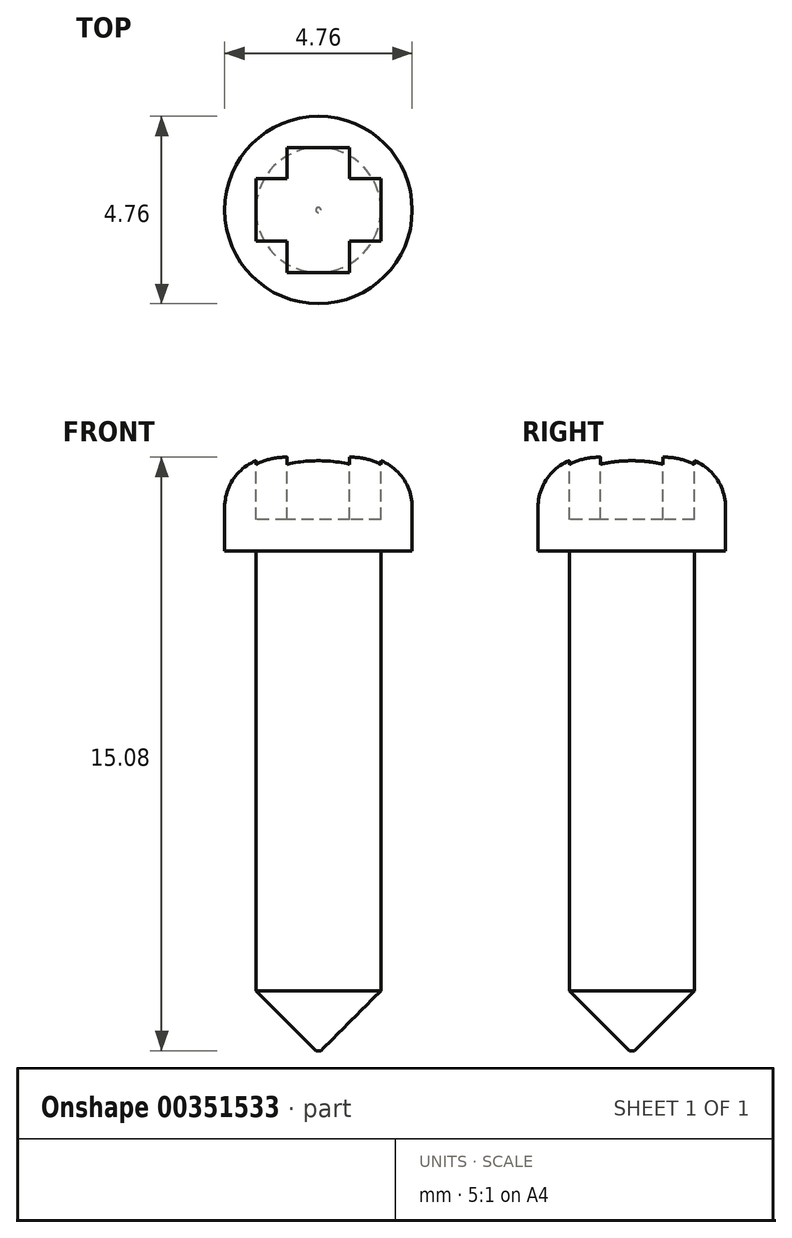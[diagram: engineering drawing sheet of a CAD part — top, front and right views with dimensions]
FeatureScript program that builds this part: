
annotation { "Feature Type Name" : "Feature", "Feature Type Description" : "" }
export const myFeature = defineFeature(function(context is Context, id is Id, definition is map)
    precondition{}
    {
        {
            var Q0;
            Q0=qCreatedBy(makeId("Top.planeOp"),FACE);
            var sketch = newSketch(context, id + "F0", { "sketchPlane" : qUnion([Q0])});
            skCircle(sketch, "E0", {"center": v(0, 0) * mm, "radius": 1.59 * mm});
            skSolve(sketch);
        }
        {
            var Q0;
            Q0 = qSketchRegion(id + "F0", true);
            extrude(context, id + "F1", {"entities" : qUnion([Q0]), "depth" : 12.7 * mm});
        }
        {
            var Q0;
            Q0=makeQuery(id+"F1.opExtrude","CAP_FACE",FACE,{"disambiguationData":[OSD([sQuery(id+"F0.wireOp",EDGE,"E0")])],"isStart":true});
            chamfer(context, id + "F2", {"entities" : qUnion([Q0]), "width" : 1.52 * mm, "tangentPropagation" : true});
        }
        {
            var Q0;
            Q0=makeQuery(id+"F1.opExtrude","CAP_FACE",FACE,{"disambiguationData":[OSD([sQuery(id+"F0.wireOp",EDGE,"E0")])],"isStart":false});
            var sketch = newSketch(context, id + "F3", { "sketchPlane" : qUnion([Q0])});
            skCircle(sketch, "E1", {"center": v(0, 0) * mm, "radius": 2.38 * mm});
            skSolve(sketch);
        }
        {
            var Q0;
            Q0 = qSketchRegion(id + "F3", true);
            extrude(context, id + "F4", {"entities" : qUnion([Q0]), "operationType" : NewBodyOperationType.ADD, "depth" : 2.38 * mm});
        }
        {
            var Q0;
            Q0=makeQuery(id+"F4.opExtrude","CAP_FACE",FACE,{"disambiguationData":[OSD([sQuery(id+"F3.wireOp",EDGE,"E1")])],"isStart":false});
            var sketch = newSketch(context, id + "F5", { "sketchPlane" : qUnion([Q0])});
            skLineSegment(sketch, "E2.bottom", {"start": v(0.8, 1.59) * mm, "end": v(-0.8, 1.59) * mm});
            skLineSegment(sketch, "E2.top", {"start": v(0.8, -1.59) * mm, "end": v(-0.8, -1.59) * mm});
            skLineSegment(sketch, "E2.left", {"start": v(0.8, 1.59) * mm, "end": v(0.8, -1.59) * mm});
            skLineSegment(sketch, "E2.right", {"start": v(-0.8, 1.59) * mm, "end": v(-0.8, -1.59) * mm});
            skPoint(sketch, "E2.middle", {"position": v(0, 0) * mm});
            skLineSegment(sketch, "E3.bottom", {"start": v(1.59, 0.8) * mm, "end": v(-1.59, 0.8) * mm});
            skLineSegment(sketch, "E3.top", {"start": v(1.59, -0.8) * mm, "end": v(-1.59, -0.8) * mm});
            skLineSegment(sketch, "E3.left", {"start": v(1.59, 0.8) * mm, "end": v(1.59, -0.8) * mm});
            skLineSegment(sketch, "E3.right", {"start": v(-1.59, 0.8) * mm, "end": v(-1.59, -0.8) * mm});
            skSolve(sketch);
        }
        {
            var Q0;
            Q0 = qSketchRegion(id + "F5", true);
            extrude(context, id + "F6", {"entities" : qUnion([Q0]), "operationType" : NewBodyOperationType.REMOVE, "oppositeDirection" : true, "depth" : 1.59 * mm});
        }
        {
            var Q0;
            Q0=makeQuery(id+"F4.opExtrude","CAP_EDGE",EDGE,{"disambiguationData":[OSD([sQuery(id+"F3.wireOp",EDGE,"E1")])],"isStart":false});
            fillet(context, id + "F7", {"entities" : qUnion([Q0]), "radius" : 1.27 * mm, "tangentPropagation" : true, "allowEdgeOverflow" : false});
        }
    });
